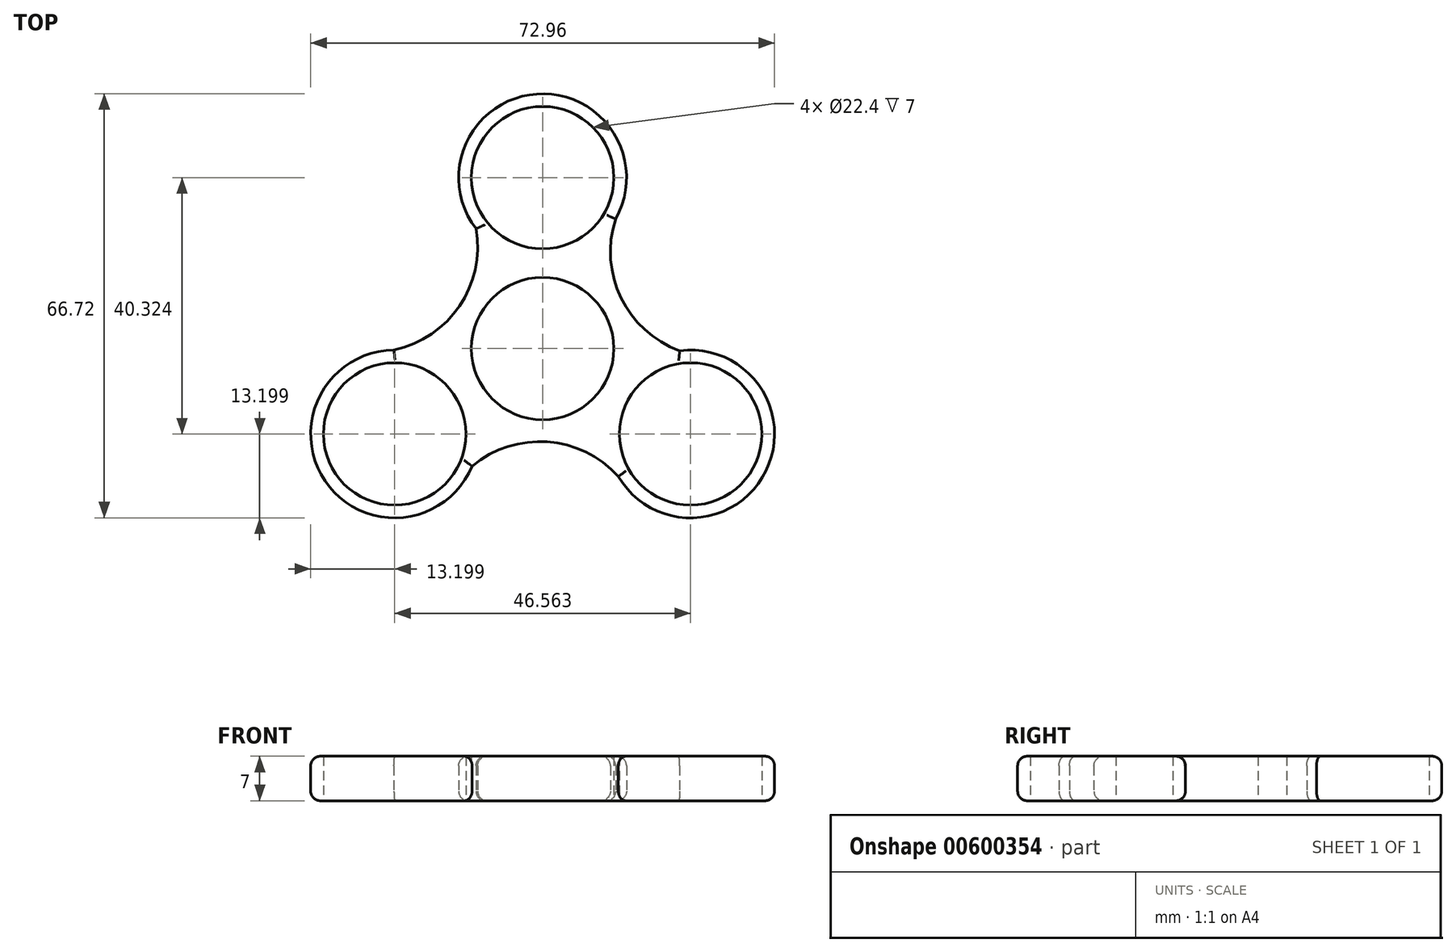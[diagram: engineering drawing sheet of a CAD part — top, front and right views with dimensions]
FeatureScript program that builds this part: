
annotation { "Feature Type Name" : "Feature", "Feature Type Description" : "" }
export const myFeature = defineFeature(function(context is Context, id is Id, definition is map)
    precondition{}
    {
        {
            var Q0;
            Q0=qCreatedBy(makeId("Top.planeOp"),FACE);
            var sketch = newSketch(context, id + "F0", { "sketchPlane" : qUnion([Q0])});
            skCircle(sketch, "E0", {"center": v(0, 0) * mm, "radius": 11.2 * mm});
            skCircle(sketch, "E1", {"center": v(0, 26.88) * mm, "radius": 11.2 * mm});
            skArc(sketch, "E2", {"start": v(11.48, 20.37) * mm, "mid": v(-0.91, 40.05) * mm, "end": v(-10.47, 18.85) * mm});
            skArc(sketch, "E3.1.0", {"start": v(-23.38, -0.24) * mm, "mid": v(-34.23, -20.82) * mm, "end": v(-11.09, -18.5) * mm});
            skCircle(sketch, "E3.1.1", {"center": v(-23.28, -13.44) * mm, "radius": 11.2 * mm});
            skArc(sketch, "E3.2.0", {"start": v(11.9, -20.13) * mm, "mid": v(35.14, -19.24) * mm, "end": v(21.56, -0.35) * mm});
            skCircle(sketch, "E3.2.1", {"center": v(23.28, -13.44) * mm, "radius": 11.2 * mm});
            skArc(sketch, "E4", {"start": v(11.48, 20.37) * mm, "mid": v(12.34, 7.98) * mm, "end": v(21.56, -0.35) * mm});
            skArc(sketch, "E5.1.0", {"start": v(-23.38, -0.24) * mm, "mid": v(-13.08, 6.7) * mm, "end": v(-10.47, 18.85) * mm});
            skArc(sketch, "E5.2.0", {"start": v(11.9, -20.13) * mm, "mid": v(0.74, -14.68) * mm, "end": v(-11.09, -18.5) * mm});
            skLineSegment(sketch, "E6.trimOffspring", {"start": v(9.58, 5.8) * mm, "end": v(12.56, 7.55) * mm, "construction": true});
            skPoint(sketch, "E7.orphan", {"position": v(45.56, 26.88) * mm});
            skSolve(sketch);
        }
        {
            var Q0;
            Q0 = qSketchRegion(id + "F0", true);
            extrude(context, id + "F1", {"entities" : qUnion([Q0]), "depth" : 7 * mm, "offsetDistance" : 25 * mm});
        }
        {
            var Q0;
            Q0=makeQuery(id+"F1.opExtrude","CAP_EDGE",EDGE,{"disambiguationData":[OSD([sQuery(id+"F0.wireOp",EDGE,"E5.2.0")])],"isStart":false});
            var Q1;
            Q1=makeQuery(id+"F1.opExtrude","CAP_EDGE",EDGE,{"disambiguationData":[OSD([sQuery(id+"F0.wireOp",EDGE,"E5.2.0")])],"isStart":true});
            fillet(context, id + "F2", {"entities" : qUnion([Q0, Q1]), "radius" : 1.5 * mm, "tangentPropagation" : true, "allowEdgeOverflow" : false});
        }
        {
            var Q0;
            Q0=makeQuery(id+"F1.opExtrude","CAP_EDGE",EDGE,{"disambiguationData":[OSD([sQuery(id+"F0.wireOp",EDGE,"E3.1.0")])],"isStart":false});
            var Q1;
            Q1=makeQuery(id+"F1.opExtrude","CAP_EDGE",EDGE,{"disambiguationData":[OSD([sQuery(id+"F0.wireOp",EDGE,"E5.1.0")])],"isStart":false});
            var Q2;
            Q2=makeQuery(id+"F1.opExtrude","CAP_EDGE",EDGE,{"disambiguationData":[OSD([sQuery(id+"F0.wireOp",EDGE,"E2")])],"isStart":false});
            var Q3;
            Q3=makeQuery(id+"F1.opExtrude","CAP_EDGE",EDGE,{"disambiguationData":[OSD([sQuery(id+"F0.wireOp",EDGE,"E4")])],"isStart":false});
            var Q4;
            Q4=makeQuery(id+"F1.opExtrude","CAP_EDGE",EDGE,{"disambiguationData":[OSD([sQuery(id+"F0.wireOp",EDGE,"E3.2.0")])],"isStart":false});
            var Q5;
            {var subQ0=sQuery(id+"F0.wireOp",EDGE,"E5.2.0");Q5=makeQuery(id+"F2.opFillet","BLEND_EDGE",EDGE,{"blendedFrom":[makeQuery(id+"F1.opExtrude","CAP_EDGE",EDGE,{"disambiguationData":[OSD([subQ0])],"isStart":false}),makeQuery(id+"F1.opExtrude","CAP_FACE",FACE,{"disambiguationData":[OSD([sQuery(id+"F0.wireOp",EDGE,"E0"),sQuery(id+"F0.wireOp",EDGE,"E1"),sQuery(id+"F0.wireOp",EDGE,"E2"),sQuery(id+"F0.wireOp",EDGE,"E3.1.0"),sQuery(id+"F0.wireOp",EDGE,"E3.1.1"),sQuery(id+"F0.wireOp",EDGE,"E3.2.0"),sQuery(id+"F0.wireOp",EDGE,"E3.2.1"),sQuery(id+"F0.wireOp",EDGE,"E4"),sQuery(id+"F0.wireOp",EDGE,"E5.1.0"),subQ0])],"isStart":false})],"blendedInto":[makeQuery(id+"F1.opExtrude","CAP_FACE",FACE,{"disambiguationData":[OSD([sQuery(id+"F0.wireOp",EDGE,"E0"),sQuery(id+"F0.wireOp",EDGE,"E1"),sQuery(id+"F0.wireOp",EDGE,"E2"),sQuery(id+"F0.wireOp",EDGE,"E3.1.0"),sQuery(id+"F0.wireOp",EDGE,"E3.1.1"),sQuery(id+"F0.wireOp",EDGE,"E3.2.0"),sQuery(id+"F0.wireOp",EDGE,"E3.2.1"),sQuery(id+"F0.wireOp",EDGE,"E4"),sQuery(id+"F0.wireOp",EDGE,"E5.1.0"),subQ0])],"isStart":false})]});}
            fillet(context, id + "F3", {"entities" : qUnion([Q0, Q1, Q2, Q3, Q4, Q5]), "radius" : 1.5 * mm, "tangentPropagation" : true, "allowEdgeOverflow" : false});
        }
        {
            var Q0;
            Q0=makeQuery(id+"F1.opExtrude","CAP_EDGE",EDGE,{"disambiguationData":[OSD([sQuery(id+"F0.wireOp",EDGE,"E3.1.0")])],"isStart":true});
            var Q1;
            Q1=makeQuery(id+"F1.opExtrude","CAP_EDGE",EDGE,{"disambiguationData":[OSD([sQuery(id+"F0.wireOp",EDGE,"E5.1.0")])],"isStart":true});
            var Q2;
            Q2=makeQuery(id+"F1.opExtrude","CAP_EDGE",EDGE,{"disambiguationData":[OSD([sQuery(id+"F0.wireOp",EDGE,"E2")])],"isStart":true});
            var Q3;
            Q3=makeQuery(id+"F1.opExtrude","CAP_EDGE",EDGE,{"disambiguationData":[OSD([sQuery(id+"F0.wireOp",EDGE,"E4")])],"isStart":true});
            var Q4;
            Q4=makeQuery(id+"F1.opExtrude","CAP_EDGE",EDGE,{"disambiguationData":[OSD([sQuery(id+"F0.wireOp",EDGE,"E3.2.0")])],"isStart":true});
            var Q5;
            {var subQ0=sQuery(id+"F0.wireOp",EDGE,"E5.2.0");Q5=makeQuery(id+"F2.opFillet","BLEND_EDGE",EDGE,{"blendedFrom":[makeQuery(id+"F1.opExtrude","CAP_EDGE",EDGE,{"disambiguationData":[OSD([subQ0])],"isStart":true}),makeQuery(id+"F1.opExtrude","CAP_FACE",FACE,{"disambiguationData":[OSD([sQuery(id+"F0.wireOp",EDGE,"E0"),sQuery(id+"F0.wireOp",EDGE,"E1"),sQuery(id+"F0.wireOp",EDGE,"E2"),sQuery(id+"F0.wireOp",EDGE,"E3.1.0"),sQuery(id+"F0.wireOp",EDGE,"E3.1.1"),sQuery(id+"F0.wireOp",EDGE,"E3.2.0"),sQuery(id+"F0.wireOp",EDGE,"E3.2.1"),sQuery(id+"F0.wireOp",EDGE,"E4"),sQuery(id+"F0.wireOp",EDGE,"E5.1.0"),subQ0])],"isStart":true})],"blendedInto":[makeQuery(id+"F1.opExtrude","CAP_FACE",FACE,{"disambiguationData":[OSD([sQuery(id+"F0.wireOp",EDGE,"E0"),sQuery(id+"F0.wireOp",EDGE,"E1"),sQuery(id+"F0.wireOp",EDGE,"E2"),sQuery(id+"F0.wireOp",EDGE,"E3.1.0"),sQuery(id+"F0.wireOp",EDGE,"E3.1.1"),sQuery(id+"F0.wireOp",EDGE,"E3.2.0"),sQuery(id+"F0.wireOp",EDGE,"E3.2.1"),sQuery(id+"F0.wireOp",EDGE,"E4"),sQuery(id+"F0.wireOp",EDGE,"E5.1.0"),subQ0])],"isStart":true})]});}
            fillet(context, id + "F4", {"entities" : qUnion([Q0, Q1, Q2, Q3, Q4, Q5]), "radius" : 1.5 * mm, "tangentPropagation" : true, "allowEdgeOverflow" : false});
        }
    });
